# Revit family: Diverter-Valve_Only_Trim-American_Standard-Universal-TU007500.002
name_source: partatom
category: Plumbing Fixtures
units: mm (PartAtom-declared; Revit-internal decimal feet)

## family parameters
Cut with Voids When Loaded = No
Host = Face
OmniClass Number = 23.45.05.14.17
OmniClass Title = Showers
Part Type = Normal
Room Calculation Point = No
Round Connector Dimension = Use Diameter
Shared = Yes

## types (1)
- TU007500.002
    ADA Compliant = Yes
    Assembly Code = D2020300
    CW Connection = Yes
    CWFU = 3
    Compliance Certifications = ANSI A117.1
    Default Elevation = 48"
    Description = UNIVERSAL Quest Valve Only Trim Kit with Lever Handle and Pressure Balance Cartridge Valve Trim only. Metal Lever Handle. LESS Valve Body
    Finish = Brass-American Standard-002-Polished Chrome
    HW Connection = Yes
    HWFU = 3
    Height = 8 1/4"
    Installation Type = Wall Mounted
    LESS Valve Body = Yes
    Manufacturer = American Standard
    Material = Brass-American Standard-002-Polished Chrome
    Model = TU007500.002
    Price = Prices may vary. Please consult Manufacturer Representative for most up-to-date price list.
    Product Documentation Link = https://americanstandard.box.com
    Product Page URL = https://www.americanstandard-us.com
    R110 Pressure Balance Rough Valve Body only = No
    R110SS Pressure Balance Rough Valve Body only with Screwdriver stops = No
    R115 Pressure Balance Rough Valve Body only = No
    R115SS Pressure Balance Rough Valve Body only with Screwdriver stops = No
    R117 Pressure Balance Rough Valve Body only = No
    R117SS Pressure Balance Rough Valve Body only with Screwdriver stops = No
    Tempered Water Connection = Yes
    URL = https://www.americanstandard-us.com
    Vent Connection = No
    WFU = 4
    Warranty Information = Limited Lifetime Warranty
    Waste Connection = No
    Width = 6 11/16"

## geometry (parser evidence)
native form markers: Sweep x3
no freeform markers — native parametric forms only
